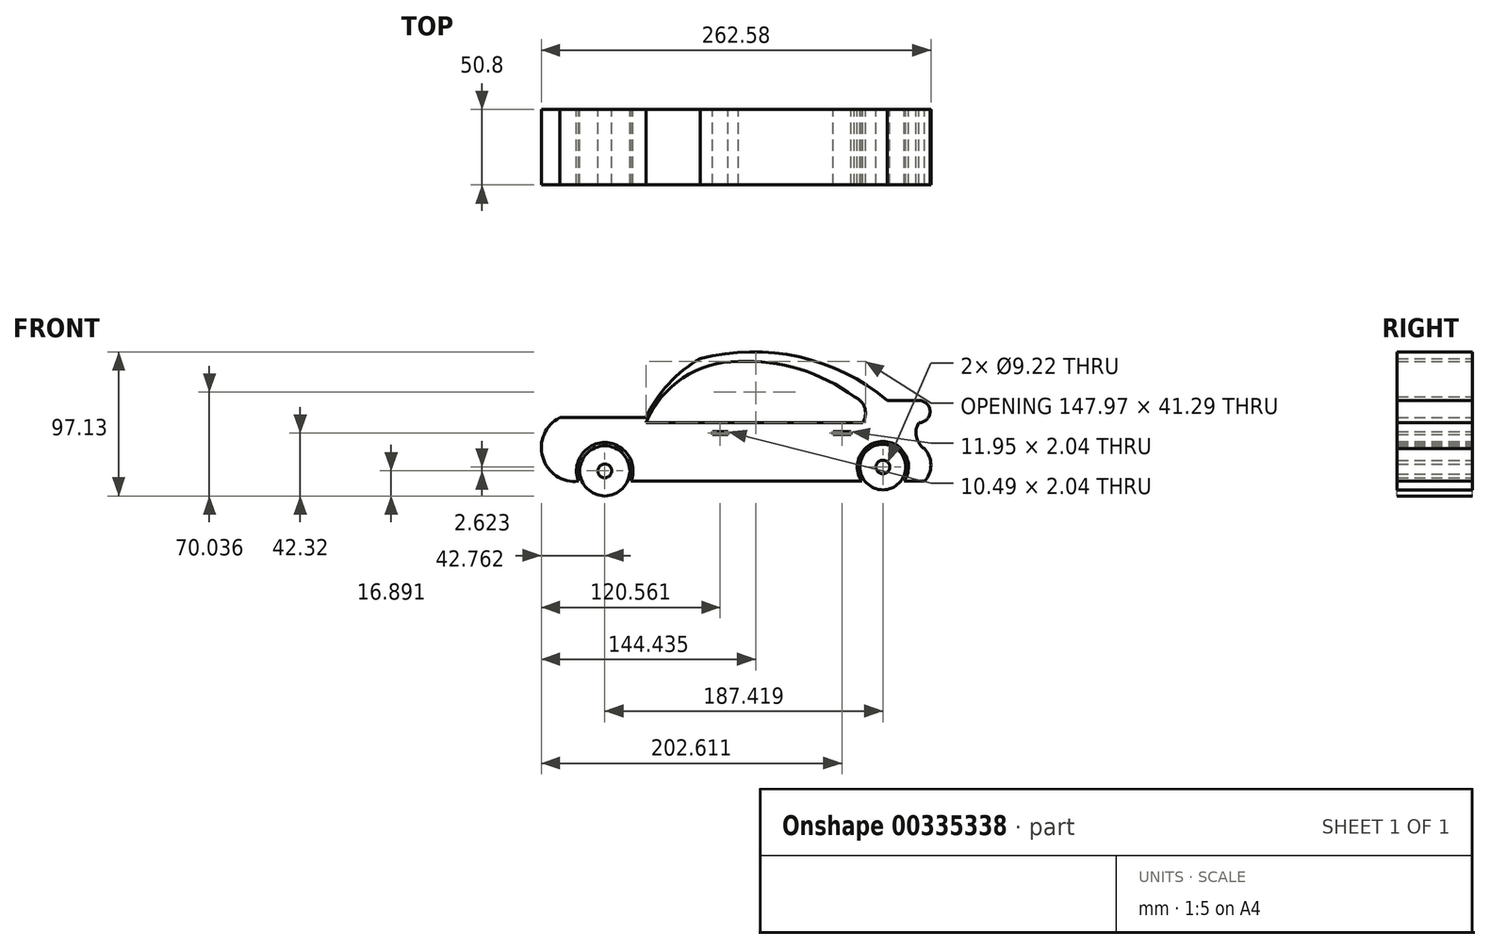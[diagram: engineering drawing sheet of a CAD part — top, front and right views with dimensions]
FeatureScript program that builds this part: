
annotation { "Feature Type Name" : "Feature", "Feature Type Description" : "" }
export const myFeature = defineFeature(function(context is Context, id is Id, definition is map)
    precondition{}
    {
        {
            var Q0;
            Q0=qCreatedBy(makeId("Front.planeOp"),FACE);
            var sketch = newSketch(context, id + "F0", { "sketchPlane" : qUnion([Q0])});
            skLineSegment(sketch, "E0", {"start": v(121.7, 15.01) * mm, "end": v(100.51, 15.01) * mm});
            skArc(sketch, "E1", {"start": v(100.51, 15.01) * mm, "mid": v(40.89, 44.31) * mm, "end": v(-25.55, 43.23) * mm});
            skArc(sketch, "E2", {"start": v(-25.55, 43.23) * mm, "mid": v(-47.04, 26.16) * mm, "end": v(-62.3, 3.35) * mm});
            skLineSegment(sketch, "E3", {"start": v(-62.3, 3.35) * mm, "end": v(-120.3, 3.35) * mm});
            skArc(sketch, "E4", {"start": v(-120.3, 3.35) * mm, "mid": v(-131.82, -23.3) * mm, "end": v(-107.71, -39.5) * mm});
            skArc(sketch, "E5", {"start": v(121.7, 0) * mm, "mid": v(129.2, 7.5) * mm, "end": v(121.7, 15.01) * mm});
            skArc(sketch, "E6", {"start": v(121.7, 0) * mm, "mid": v(120.03, -9.53) * mm, "end": v(125.37, -17.59) * mm});
            skArc(sketch, "E7", {"start": v(125.37, -39.5) * mm, "mid": v(129.84, -28.54) * mm, "end": v(125.37, -17.59) * mm});
            skLineSegment(sketch, "E8", {"start": v(125.37, -39.5) * mm, "end": v(111.76, -39.5) * mm});
            skArc(sketch, "E9", {"start": v(111.76, -39.5) * mm, "mid": v(97.44, -12.63) * mm, "end": v(83.12, -39.5) * mm});
            skArc(sketch, "E10", {"start": v(-72.24, -39.5) * mm, "mid": v(-89.98, -13.44) * mm, "end": v(-107.71, -39.5) * mm});
            skLineSegment(sketch, "E11", {"start": v(-72.24, -39.5) * mm, "end": v(83.12, -39.5) * mm});
            skLineSegment(sketch, "E12", {"start": v(-62.3, 0) * mm, "end": v(-62.3, -39.5) * mm});
            skArc(sketch, "E13", {"start": v(0, 41.24) * mm, "mid": v(-37.36, 30.01) * mm, "end": v(-62.3, 0) * mm});
            skArc(sketch, "E14", {"start": v(78.2, 17.34) * mm, "mid": v(41.18, 36.1) * mm, "end": v(0, 41.24) * mm});
            skLineSegment(sketch, "E15", {"start": v(-62.3, 0) * mm, "end": v(83.74, 0) * mm});
            skArc(sketch, "E16", {"start": v(83.74, 0) * mm, "mid": v(85.17, 10.01) * mm, "end": v(78.2, 17.34) * mm});
            skLineSegment(sketch, "E17", {"start": v(78.2, 17.34) * mm, "end": v(83.74, 0) * mm});
            skArc(sketch, "E18", {"start": v(83.16, -13.26) * mm, "mid": v(85.02, -6.7) * mm, "end": v(83.74, 0) * mm});
            skLineSegment(sketch, "E19", {"start": v(83.16, -13.26) * mm, "end": v(64.5, -39.5) * mm});
            skLineSegment(sketch, "E20", {"start": v(0, 0) * mm, "end": v(0, -39.5) * mm});
            skLineSegment(sketch, "E21", {"start": v(0, 0) * mm, "end": v(0, 41.24) * mm});
            skCircle(sketch, "E22", {"center": v(-89.98, -32.5) * mm, "radius": 16.89 * mm});
            skCircle(sketch, "E23", {"center": v(97.44, -29.88) * mm, "radius": 15.4 * mm});
            skCircle(sketch, "E24", {"center": v(-89.98, -32.5) * mm, "radius": 4.6 * mm});
            skCircle(sketch, "E25", {"center": v(97.44, -29.88) * mm, "radius": 4.6 * mm});
            skLineSegment(sketch, "E26", {"start": v(-17.43, -6.05) * mm, "end": v(-6.93, -6.05) * mm});
            skLineSegment(sketch, "E27", {"start": v(-17.43, -8.1) * mm, "end": v(-6.93, -8.1) * mm});
            skLineSegment(sketch, "E28", {"start": v(63.9, -6.05) * mm, "end": v(75.85, -6.05) * mm});
            skLineSegment(sketch, "E29", {"start": v(63.9, -8.1) * mm, "end": v(75.85, -8.1) * mm});
            skLineSegment(sketch, "E30", {"start": v(-17.43, -6.05) * mm, "end": v(-17.43, -8.1) * mm});
            skLineSegment(sketch, "E31", {"start": v(-6.93, -6.05) * mm, "end": v(-6.93, -8.1) * mm});
            skLineSegment(sketch, "E32", {"start": v(63.9, -6.05) * mm, "end": v(63.9, -8.1) * mm});
            skLineSegment(sketch, "E33", {"start": v(75.85, -6.05) * mm, "end": v(75.85, -8.1) * mm});
            skLineSegment(sketch, "E34", {"start": v(-128.54, -3.75) * mm, "end": v(-103.39, -3.75) * mm});
            skArc(sketch, "E35", {"start": v(-110.03, -16.9) * mm, "mid": v(-104.7, -11.35) * mm, "end": v(-103.39, -3.75) * mm});
            skLineSegment(sketch, "E36", {"start": v(-110.03, -16.9) * mm, "end": v(-132.74, -16.9) * mm});
            skSolve(sketch);
        }
        {
            var Q0;
            {var subQ0=sQuery(id+"F0.wireOp",EDGE,"E34");Q0=makeQuery(id+"F0.imprint","IMPRINT",FACE,{"disambiguationData":[TD([[makeQuery(id+"F0.imprint","IMPRINT",EDGE,{"derivedFrom":subQ0}),-1.0]])]});}
            var Q1;
            Q1=makeQuery(id+"F0.imprint","IMPRINT",FACE,{"disambiguationData":[TD([[makeQuery(id+"F0.imprint","IMPRINT",EDGE,{"derivedFrom":sQuery(id+"F0.wireOp",EDGE,"E22")}),1.0]])]});
            var Q2;
            Q2=makeQuery(id+"F0.imprint","IMPRINT",FACE,{"disambiguationData":[TD([[makeQuery(id+"F0.imprint","IMPRINT",EDGE,{"derivedFrom":sQuery(id+"F0.wireOp",EDGE,"E23")}),1.0]])]});
            var Q3;
            {var subQ0=sQuery(id+"F0.wireOp",EDGE,"E18");Q3=makeQuery(id+"F0.imprint","IMPRINT",FACE,{"disambiguationData":[TD([[makeQuery(id+"F0.imprint","IMPRINT",EDGE,{"derivedFrom":subQ0}),1.0]])]});}
            var Q4;
            {var subQ2=sQuery(id+"F0.wireOp",EDGE,"E12");Q4=makeQuery(id+"F0.imprint","IMPRINT",FACE,{"disambiguationData":[TD([[makeQuery(id+"F0.imprint","IMPRINT",EDGE,{"derivedFrom":subQ2}),1.0]])]});}
            var Q5;
            Q5=makeQuery(id+"F0.imprint","IMPRINT",FACE,{"disambiguationData":[TD([[makeQuery(id+"F0.imprint","IMPRINT",EDGE,{"derivedFrom":sQuery(id+"F0.wireOp",EDGE,"E0")}),1.0]])]});
            extrude(context, id + "F1", {"entities" : qUnion([Q0, Q1, Q2, Q3, Q4, Q5]), "depth" : 50.8 * mm});
        }
    });
